# Revit family: OASIS SH-4836 STD
name_source: partatom
category: Plumbing Fixtures
revit_build: Autodesk Revit 2013 (Build: 20130531_2115(x64)
units: mm (PartAtom-declared; Revit-internal decimal feet)

## types (7) — shared parameters
BIM Model By = www.epoch-design.com
Color = <By Category>
Grab Bar Finish = <By Category>
Manufacturer = OASIS
Sanitary Connector = Sanitary Connection
Sanitary Radius = 0' - 1 11/16"
Seat Finish = <By Category>
Stainless steel = <By Category>
Type Comments = SHOWER
URL = www.oasisbath.com

## per-type parameters (varying)
| type | Bar_Horz_Back | Bar_Horz_Left | Bar_Horz_Right | Bar_Vert | Model | Seat_Fold |
| BP1 package | Yes | Yes | No | No | SH-4836 STD/BP1 | No |
| Base Model, 3SF, 3SM, & FH packages | No | No | No | No | SH-4836 STD/(3SF,3SM,FH) | No |
| BP2 package | Yes | Yes | No | Yes | SH-4836 STD/BP2 | No |
| BP3 package | Yes | Yes | Yes | No | SH-4836 STD/BP3 | No |
| BP5 package | Yes | No | No | No | SH-4836 STD/BP5 | No |
| TL package | Yes | Yes | No | No | SH-4836 STD/TL | Yes |
| TLV package | Yes | Yes | No | Yes | SH-4836 STD/TLV | Yes |

## geometry (parser evidence)
native form markers: Sweep x11
no freeform markers — native parametric forms only
